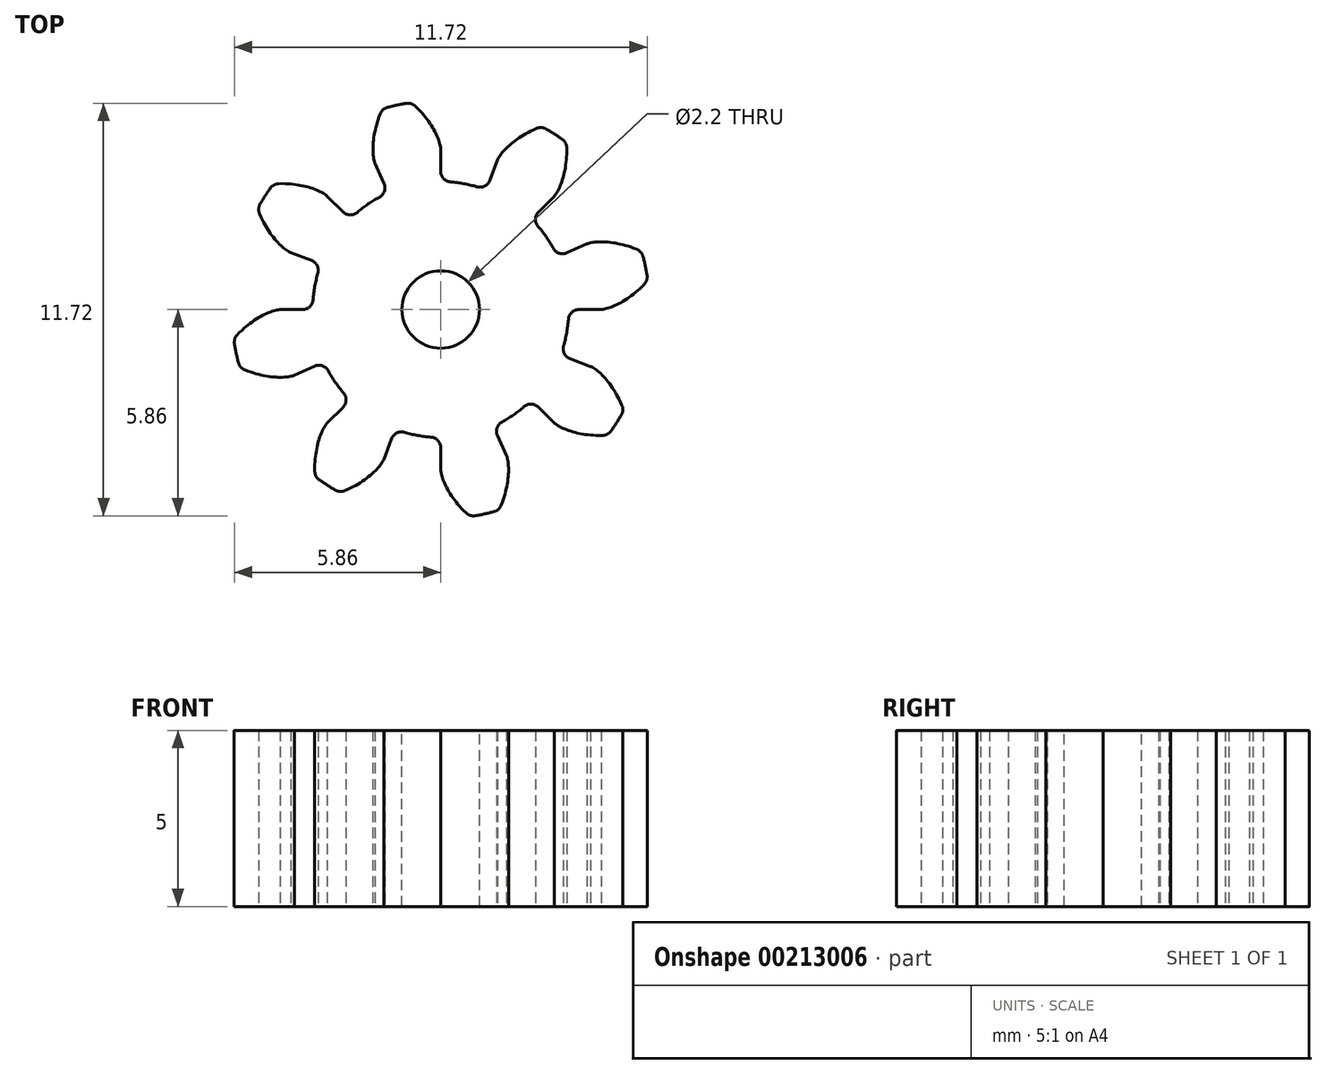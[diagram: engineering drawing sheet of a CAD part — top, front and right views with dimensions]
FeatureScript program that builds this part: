
annotation { "Feature Type Name" : "Feature", "Feature Type Description" : "" }
export const myFeature = defineFeature(function(context is Context, id is Id, definition is map)
    precondition{}
    {
        {
            var Q0;
            Q0=qCreatedBy(makeId("Top.planeOp"),FACE);
            var sketch = newSketch(context, id + "F0", { "sketchPlane" : qUnion([Q0])});
            skCircle(sketch, "E0", {"center": v(0, 0) * mm, "radius": 4.56 * mm, "construction": true});
            skLineSegment(sketch, "E1", {"start": v(0, 0) * mm, "end": v(4.54, 0.39) * mm, "construction": true});
            skLineSegment(sketch, "E2", {"start": v(4.54, 0.39) * mm, "end": v(4.57, 0) * mm, "construction": true});
            skLineSegment(sketch, "E3", {"start": v(0, 0) * mm, "end": v(4.5, 0.77) * mm, "construction": true});
            skLineSegment(sketch, "E4", {"start": v(4.5, 0.77) * mm, "end": v(4.62, 0) * mm, "construction": true});
            skLineSegment(sketch, "E5", {"start": v(0, 0) * mm, "end": v(4.4, 1.14) * mm, "construction": true});
            skLineSegment(sketch, "E6", {"start": v(4.4, 1.14) * mm, "end": v(4.7, 0.02) * mm, "construction": true});
            skLineSegment(sketch, "E7", {"start": v(0, 0) * mm, "end": v(4.3, 1.51) * mm, "construction": true});
            skLineSegment(sketch, "E8", {"start": v(4.3, 1.51) * mm, "end": v(4.8, 0.06) * mm, "construction": true});
            skLineSegment(sketch, "E9", {"start": v(0, 0) * mm, "end": v(4.15, 1.87) * mm, "construction": true});
            skLineSegment(sketch, "E10", {"start": v(4.15, 1.87) * mm, "end": v(4.95, 0.11) * mm, "construction": true});
            skLineSegment(sketch, "E11", {"start": v(0, 0) * mm, "end": v(3.98, 2.22) * mm, "construction": true});
            skLineSegment(sketch, "E12", {"start": v(3.98, 2.22) * mm, "end": v(5.1, 0.2) * mm, "construction": true});
            skLineSegment(sketch, "E13", {"start": v(0, 0) * mm, "end": v(3.78, 2.54) * mm, "construction": true});
            skLineSegment(sketch, "E14", {"start": v(3.78, 2.54) * mm, "end": v(5.29, 0.3) * mm, "construction": true});
            skLineSegment(sketch, "E15", {"start": v(0, 0) * mm, "end": v(3.55, 2.85) * mm, "construction": true});
            skLineSegment(sketch, "E16", {"start": v(3.55, 2.85) * mm, "end": v(5.48, 0.45) * mm, "construction": true});
            skLineSegment(sketch, "E17", {"start": v(0, 0) * mm, "end": v(3.3, 3.14) * mm, "construction": true});
            skLineSegment(sketch, "E18", {"start": v(3.3, 3.14) * mm, "end": v(5.7, 0.63) * mm, "construction": true});
            skLineSegment(sketch, "E19", {"start": v(0, 0) * mm, "end": v(3.02, 3.41) * mm, "construction": true});
            skLineSegment(sketch, "E20", {"start": v(3.02, 3.41) * mm, "end": v(5.9, 0.86) * mm, "construction": true});
            skLineSegment(sketch, "E21", {"start": v(0, 0) * mm, "end": v(13.15, 2.82) * mm, "construction": true});
            skPoint(sketch, "E22", {"position": v(4.56, 0) * mm});
            skFitSpline(sketch, "E23", {"points": [v(4.56, 0) * mm, v(4.57, 0) * mm, v(4.62, 0) * mm, v(4.7, 0.02) * mm, v(4.8, 0.06) * mm, v(4.95, 0.11) * mm, v(5.1, 0.2) * mm, v(5.29, 0.3) * mm, v(5.48, 0.45) * mm, v(5.7, 0.63) * mm, v(5.9, 0.86) * mm], "startDerivative": vector(0.23, 0.05) * mm, "endDerivative": vector(0.8, 0.9) * mm});
            skFitSpline(sketch, "E24.MirrorCS", {"points": [v(4.16, 1.87) * mm, v(4.17, 1.87) * mm, v(4.22, 1.89) * mm, v(4.3, 1.9) * mm, v(4.41, 1.92) * mm, v(4.56, 1.92) * mm, v(4.74, 1.92) * mm, v(4.95, 1.89) * mm, v(5.19, 1.84) * mm, v(5.45, 1.76) * mm, v(5.74, 1.64) * mm], "startDerivative": vector(0.24, 0.05) * mm, "endDerivative": vector(1.1, -0.5) * mm});
            skCircle(sketch, "E25", {"center": v(0, 0) * mm, "radius": 3.64 * mm});
            skLineSegment(sketch, "E26", {"start": v(4.16, 1.87) * mm, "end": v(3.32, 1.5) * mm});
            skLineSegment(sketch, "E27", {"start": v(4.56, 0) * mm, "end": v(3.64, 0) * mm});
            skArc(sketch, "E28", {"start": v(5.7, 1.66) * mm, "mid": v(-5.8, -1.25) * mm, "end": v(5.88, 0.83) * mm, "construction": true});
            skArc(sketch, "E29", {"start": v(5.88, 0.83) * mm, "mid": v(5.8, 1.25) * mm, "end": v(5.7, 1.66) * mm});
            skSolve(sketch);
        }
        {
            var Q0;
            {var subQ0=sQuery(id+"F0.wireOp",EDGE,"E25");var subQ1=makeQuery(id+"F0.imprint","INTERSECT",VERTEX,{"derivedFrom":[subQ0,sQuery(id+"F0.wireOp",EDGE,"E26")]});Q0=makeQuery(id+"F0.imprint","IMPRINT",FACE,{"disambiguationData":[TD([[makeQuery(id+"F0.imprint","IMPRINT",EDGE,{"disambiguationData":[TD([[subQ1,1.0]])],"derivedFrom":subQ0}),1.0]])]});}
            var Q1;
            {var subQ0=sQuery(id+"F0.wireOp",EDGE,"E26");Q1=makeQuery(id+"F0.imprint","IMPRINT",FACE,{"disambiguationData":[TD([[makeQuery(id+"F0.imprint","IMPRINT",EDGE,{"derivedFrom":subQ0}),1.0]])]});}
            extrude(context, id + "F1", {"entities" : qUnion([Q0, Q1]), "depth" : 5 * mm});
        }
        {
            var Q0;
            Q0=qCreatedBy(makeId("Front.planeOp"),FACE);
            var sketch = newSketch(context, id + "F2", { "sketchPlane" : qUnion([Q0])});
            skLineSegment(sketch, "E30", {"start": v(0, 17.16) * mm, "end": v(0, -23.29) * mm});
            skSolve(sketch);
        }
        {
            var Q0;
            Q0=makeQuery(id+"F1.opExtrude","SWEPT_EDGE",EDGE,{"disambiguationData":[OSD([sQuery(id+"F0.wireOp",EDGE,"E23"),sQuery(id+"F0.wireOp",EDGE,"E29")])]});
            var Q1;
            Q1=makeQuery(id+"F1.opExtrude","SWEPT_EDGE",EDGE,{"disambiguationData":[OSD([sQuery(id+"F0.wireOp",EDGE,"E24.MirrorCS"),sQuery(id+"F0.wireOp",EDGE,"E29")])]});
            var Q2;
            Q2=makeQuery(id+"F1.opExtrude","SWEPT_EDGE",EDGE,{"disambiguationData":[OSD([sQuery(id+"F0.wireOp",EDGE,"E25"),sQuery(id+"F0.wireOp",EDGE,"E26")])]});
            var Q3;
            Q3=makeQuery(id+"F1.opExtrude","SWEPT_EDGE",EDGE,{"disambiguationData":[OSD([sQuery(id+"F0.wireOp",EDGE,"E25"),sQuery(id+"F0.wireOp",EDGE,"E27")])]});
            fillet(context, id + "F3", {"entities" : qUnion([Q0, Q1, Q2, Q3]), "radius" : 0.3 * mm, "tangentPropagation" : true, "allowEdgeOverflow" : false});
        }
        {
            var Q0;
            Q0=makeQuery(id+"F1.opExtrude","SWEPT_BODY",BODY,{"disambiguationData":[OSD([sQuery(id+"F0.wireOp",EDGE,"E23"),sQuery(id+"F0.wireOp",EDGE,"E24.MirrorCS"),sQuery(id+"F0.wireOp",EDGE,"1a299645-abdb-4f32-9ee9-ecc138966a6f2"),sQuery(id+"F0.wireOp",EDGE,"jVUKNfs0-U7P9-c27y-fPl9-bbkh1dClkgCd"),sQuery(id+"F0.wireOp",EDGE,"61YPa2sE-s3Wu-mmsz-h82s-RpTTf0lVN2Gj"),sQuery(id+"F0.wireOp",EDGE,"0d775b13-9e2e-4655-ae11-557f0cefb09c1")])]});
            var Q1;
            Q1=sQuery(id+"F2.wireOp",EDGE,"E30");
            circularPattern(context, id + "F4", {"operationType" : NewBodyOperationType.ADD, "entities" : qUnion([Q0]), "axis" : qUnion([Q1]), "angle" : 360 * degree, "instanceCount" : 8, "equalSpace" : true});
        }
        {
            var Q0;
            {var subQ0=makeQuery(id+"F1.opExtrude","CAP_FACE",FACE,{"disambiguationData":[OSD([sQuery(id+"F0.wireOp",EDGE,"E23"),sQuery(id+"F0.wireOp",EDGE,"E24.MirrorCS"),sQuery(id+"F0.wireOp",EDGE,"1a299645-abdb-4f32-9ee9-ecc138966a6f2"),sQuery(id+"F0.wireOp",EDGE,"jVUKNfs0-U7P9-c27y-fPl9-bbkh1dClkgCd"),sQuery(id+"F0.wireOp",EDGE,"61YPa2sE-s3Wu-mmsz-h82s-RpTTf0lVN2Gj"),sQuery(id+"F0.wireOp",EDGE,"0d775b13-9e2e-4655-ae11-557f0cefb09c1")])],"isStart":false});Q0=makeQuery(id+"F4.boolean.opBoolean","MERGE",FACE,{"derivedFrom":[subQ0,makeQuery(id+"F4.opPattern","COPY",FACE,{"derivedFrom":subQ0,"instanceName":"1"}),makeQuery(id+"F4.opPattern","COPY",FACE,{"derivedFrom":subQ0,"instanceName":"2"}),makeQuery(id+"F4.opPattern","COPY",FACE,{"derivedFrom":subQ0,"instanceName":"3"}),makeQuery(id+"F4.opPattern","COPY",FACE,{"derivedFrom":subQ0,"instanceName":"4"}),makeQuery(id+"F4.opPattern","COPY",FACE,{"derivedFrom":subQ0,"instanceName":"5"}),makeQuery(id+"F4.opPattern","COPY",FACE,{"derivedFrom":subQ0,"instanceName":"6"}),makeQuery(id+"F4.opPattern","COPY",FACE,{"derivedFrom":subQ0,"instanceName":"7"}),makeQuery(id+"F4.opPattern","COPY",FACE,{"derivedFrom":subQ0,"instanceName":"8"}),makeQuery(id+"F4.opPattern","COPY",FACE,{"derivedFrom":subQ0,"instanceName":"9"}),makeQuery(id+"F4.opPattern","COPY",FACE,{"derivedFrom":subQ0,"instanceName":"10"}),makeQuery(id+"F4.opPattern","COPY",FACE,{"derivedFrom":subQ0,"instanceName":"11"}),makeQuery(id+"F4.opPattern","COPY",FACE,{"derivedFrom":subQ0,"instanceName":"12"}),makeQuery(id+"F4.opPattern","COPY",FACE,{"derivedFrom":subQ0,"instanceName":"13"}),makeQuery(id+"F4.opPattern","COPY",FACE,{"derivedFrom":subQ0,"instanceName":"14"}),makeQuery(id+"F4.opPattern","COPY",FACE,{"derivedFrom":subQ0,"instanceName":"15"})]});}
            var sketch = newSketch(context, id + "F5", { "sketchPlane" : qUnion([Q0])});
            skCircle(sketch, "E31", {"center": v(0, 0) * mm, "radius": 1.1 * mm});
            skSolve(sketch);
        }
        {
            var Q0;
            Q0=makeQuery(id+"F5.imprint","IMPRINT",FACE,{"disambiguationData":[TD([[makeQuery(id+"F5.imprint","IMPRINT",EDGE,{"derivedFrom":sQuery(id+"F5.wireOp",EDGE,"E31")}),1.0]])]});
            extrude(context, id + "F6", {"entities" : qUnion([Q0]), "operationType" : NewBodyOperationType.REMOVE, "endBound" : BoundingType.THROUGH_ALL, "oppositeDirection" : true, "depth" : 25 * mm});
        }
    });
